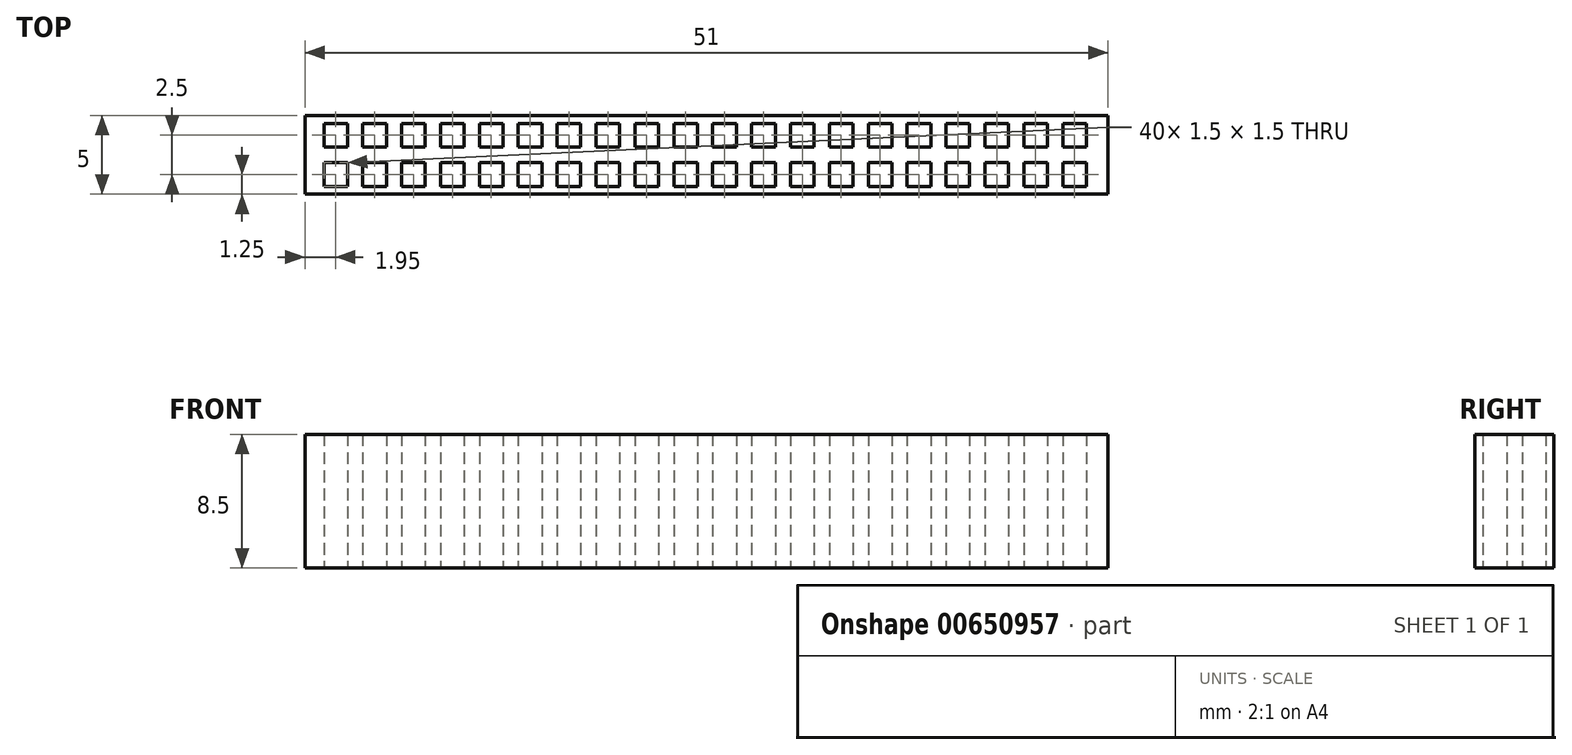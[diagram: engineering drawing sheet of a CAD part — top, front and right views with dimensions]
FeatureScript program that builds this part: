
annotation { "Feature Type Name" : "Feature", "Feature Type Description" : "" }
export const myFeature = defineFeature(function(context is Context, id is Id, definition is map)
    precondition{}
    {
        {
            var Q0;
            Q0=qCreatedBy(makeId("Top.planeOp"),FACE);
            var sketch = newSketch(context, id + "F0", { "sketchPlane" : qUnion([Q0])});
            skLineSegment(sketch, "E0.bottom", {"start": v(0, 0) * mm, "end": v(51, 0) * mm});
            skLineSegment(sketch, "E0.top", {"start": v(0, 5) * mm, "end": v(51, 5) * mm});
            skLineSegment(sketch, "E0.left", {"start": v(0, 0) * mm, "end": v(0, 5) * mm});
            skLineSegment(sketch, "E0.right", {"start": v(51, 0) * mm, "end": v(51, 5) * mm});
            skLineSegment(sketch, "E1.bottom", {"start": v(1.2, 0.5) * mm, "end": v(2.7, 0.5) * mm});
            skLineSegment(sketch, "E1.top", {"start": v(1.2, 2) * mm, "end": v(2.7, 2) * mm});
            skLineSegment(sketch, "E1.left", {"start": v(1.2, 0.5) * mm, "end": v(1.2, 2) * mm});
            skLineSegment(sketch, "E1.right", {"start": v(2.7, 0.5) * mm, "end": v(2.7, 2) * mm});
            skLineSegment(sketch, "E2.0.1.0", {"start": v(1.2, 3) * mm, "end": v(2.7, 3) * mm});
            skLineSegment(sketch, "E2.0.1.1", {"start": v(2.7, 3) * mm, "end": v(2.7, 4.5) * mm});
            skLineSegment(sketch, "E2.0.1.2", {"start": v(1.2, 4.5) * mm, "end": v(2.7, 4.5) * mm});
            skLineSegment(sketch, "E2.0.1.3", {"start": v(1.2, 3) * mm, "end": v(1.2, 4.5) * mm});
            skLineSegment(sketch, "E2.1.0.0", {"start": v(3.67, 0.5) * mm, "end": v(5.17, 0.5) * mm});
            skLineSegment(sketch, "E2.1.0.1", {"start": v(5.17, 0.5) * mm, "end": v(5.17, 2) * mm});
            skLineSegment(sketch, "E2.1.0.2", {"start": v(3.67, 2) * mm, "end": v(5.17, 2) * mm});
            skLineSegment(sketch, "E2.1.0.3", {"start": v(3.67, 0.5) * mm, "end": v(3.67, 2) * mm});
            skLineSegment(sketch, "E2.1.1.0", {"start": v(3.67, 3) * mm, "end": v(5.17, 3) * mm});
            skLineSegment(sketch, "E2.1.1.1", {"start": v(5.17, 3) * mm, "end": v(5.17, 4.5) * mm});
            skLineSegment(sketch, "E2.1.1.2", {"start": v(3.67, 4.5) * mm, "end": v(5.17, 4.5) * mm});
            skLineSegment(sketch, "E2.1.1.3", {"start": v(3.67, 3) * mm, "end": v(3.67, 4.5) * mm});
            skLineSegment(sketch, "E2.2.0.0", {"start": v(6.14, 0.5) * mm, "end": v(7.64, 0.5) * mm});
            skLineSegment(sketch, "E2.2.0.1", {"start": v(7.64, 0.5) * mm, "end": v(7.64, 2) * mm});
            skLineSegment(sketch, "E2.2.0.2", {"start": v(6.14, 2) * mm, "end": v(7.64, 2) * mm});
            skLineSegment(sketch, "E2.2.0.3", {"start": v(6.14, 0.5) * mm, "end": v(6.14, 2) * mm});
            skLineSegment(sketch, "E2.2.1.0", {"start": v(6.14, 3) * mm, "end": v(7.64, 3) * mm});
            skLineSegment(sketch, "E2.2.1.1", {"start": v(7.64, 3) * mm, "end": v(7.64, 4.5) * mm});
            skLineSegment(sketch, "E2.2.1.2", {"start": v(6.14, 4.5) * mm, "end": v(7.64, 4.5) * mm});
            skLineSegment(sketch, "E2.2.1.3", {"start": v(6.14, 3) * mm, "end": v(6.14, 4.5) * mm});
            skLineSegment(sketch, "E2.direction1", {"start": v(1.2, 0.5) * mm, "end": v(3.67, 0.5) * mm, "construction": true});
            skLineSegment(sketch, "E2.direction2", {"start": v(1.2, 0.5) * mm, "end": v(1.2, 3) * mm, "construction": true});
            skLineSegment(sketch, "E3.0.3.0", {"start": v(8.61, 0.5) * mm, "end": v(10.11, 0.5) * mm});
            skLineSegment(sketch, "E3.3.3.0", {"start": v(10.11, 0.5) * mm, "end": v(10.11, 2) * mm});
            skLineSegment(sketch, "E3.6.3.0", {"start": v(8.61, 2) * mm, "end": v(10.11, 2) * mm});
            skLineSegment(sketch, "E3.9.3.0", {"start": v(8.61, 0.5) * mm, "end": v(8.61, 2) * mm});
            skLineSegment(sketch, "E3.0.3.1", {"start": v(8.61, 3) * mm, "end": v(10.11, 3) * mm});
            skLineSegment(sketch, "E3.3.3.1", {"start": v(10.11, 3) * mm, "end": v(10.11, 4.5) * mm});
            skLineSegment(sketch, "E3.6.3.1", {"start": v(8.61, 4.5) * mm, "end": v(10.11, 4.5) * mm});
            skLineSegment(sketch, "E3.9.3.1", {"start": v(8.61, 3) * mm, "end": v(8.61, 4.5) * mm});
            skLineSegment(sketch, "E3.0.4.0", {"start": v(11.08, 0.5) * mm, "end": v(12.58, 0.5) * mm});
            skLineSegment(sketch, "E3.3.4.0", {"start": v(12.58, 0.5) * mm, "end": v(12.58, 2) * mm});
            skLineSegment(sketch, "E3.6.4.0", {"start": v(11.08, 2) * mm, "end": v(12.58, 2) * mm});
            skLineSegment(sketch, "E3.9.4.0", {"start": v(11.08, 0.5) * mm, "end": v(11.08, 2) * mm});
            skLineSegment(sketch, "E3.0.4.1", {"start": v(11.08, 3) * mm, "end": v(12.58, 3) * mm});
            skLineSegment(sketch, "E3.3.4.1", {"start": v(12.58, 3) * mm, "end": v(12.58, 4.5) * mm});
            skLineSegment(sketch, "E3.6.4.1", {"start": v(11.08, 4.5) * mm, "end": v(12.58, 4.5) * mm});
            skLineSegment(sketch, "E3.9.4.1", {"start": v(11.08, 3) * mm, "end": v(11.08, 4.5) * mm});
            skLineSegment(sketch, "E3.0.5.0", {"start": v(13.55, 0.5) * mm, "end": v(15.05, 0.5) * mm});
            skLineSegment(sketch, "E3.3.5.0", {"start": v(15.05, 0.5) * mm, "end": v(15.05, 2) * mm});
            skLineSegment(sketch, "E3.6.5.0", {"start": v(13.55, 2) * mm, "end": v(15.05, 2) * mm});
            skLineSegment(sketch, "E3.9.5.0", {"start": v(13.55, 0.5) * mm, "end": v(13.55, 2) * mm});
            skLineSegment(sketch, "E3.0.5.1", {"start": v(13.55, 3) * mm, "end": v(15.05, 3) * mm});
            skLineSegment(sketch, "E3.3.5.1", {"start": v(15.05, 3) * mm, "end": v(15.05, 4.5) * mm});
            skLineSegment(sketch, "E3.6.5.1", {"start": v(13.55, 4.5) * mm, "end": v(15.05, 4.5) * mm});
            skLineSegment(sketch, "E3.9.5.1", {"start": v(13.55, 3) * mm, "end": v(13.55, 4.5) * mm});
            skLineSegment(sketch, "E3.0.6.0", {"start": v(16.02, 0.5) * mm, "end": v(17.52, 0.5) * mm});
            skLineSegment(sketch, "E3.3.6.0", {"start": v(17.52, 0.5) * mm, "end": v(17.52, 2) * mm});
            skLineSegment(sketch, "E3.6.6.0", {"start": v(16.02, 2) * mm, "end": v(17.52, 2) * mm});
            skLineSegment(sketch, "E3.9.6.0", {"start": v(16.02, 0.5) * mm, "end": v(16.02, 2) * mm});
            skLineSegment(sketch, "E3.0.6.1", {"start": v(16.02, 3) * mm, "end": v(17.52, 3) * mm});
            skLineSegment(sketch, "E3.3.6.1", {"start": v(17.52, 3) * mm, "end": v(17.52, 4.5) * mm});
            skLineSegment(sketch, "E3.6.6.1", {"start": v(16.02, 4.5) * mm, "end": v(17.52, 4.5) * mm});
            skLineSegment(sketch, "E3.9.6.1", {"start": v(16.02, 3) * mm, "end": v(16.02, 4.5) * mm});
            skLineSegment(sketch, "E3.0.7.0", {"start": v(18.5, 0.5) * mm, "end": v(20, 0.5) * mm});
            skLineSegment(sketch, "E3.3.7.0", {"start": v(20, 0.5) * mm, "end": v(20, 2) * mm});
            skLineSegment(sketch, "E3.6.7.0", {"start": v(18.5, 2) * mm, "end": v(20, 2) * mm});
            skLineSegment(sketch, "E3.9.7.0", {"start": v(18.5, 0.5) * mm, "end": v(18.5, 2) * mm});
            skLineSegment(sketch, "E3.0.7.1", {"start": v(18.5, 3) * mm, "end": v(20, 3) * mm});
            skLineSegment(sketch, "E3.3.7.1", {"start": v(20, 3) * mm, "end": v(20, 4.5) * mm});
            skLineSegment(sketch, "E3.6.7.1", {"start": v(18.5, 4.5) * mm, "end": v(20, 4.5) * mm});
            skLineSegment(sketch, "E3.9.7.1", {"start": v(18.5, 3) * mm, "end": v(18.5, 4.5) * mm});
            skLineSegment(sketch, "E3.0.8.0", {"start": v(20.96, 0.5) * mm, "end": v(22.46, 0.5) * mm});
            skLineSegment(sketch, "E3.3.8.0", {"start": v(22.46, 0.5) * mm, "end": v(22.46, 2) * mm});
            skLineSegment(sketch, "E3.6.8.0", {"start": v(20.96, 2) * mm, "end": v(22.46, 2) * mm});
            skLineSegment(sketch, "E3.9.8.0", {"start": v(20.96, 0.5) * mm, "end": v(20.96, 2) * mm});
            skLineSegment(sketch, "E3.0.8.1", {"start": v(20.96, 3) * mm, "end": v(22.46, 3) * mm});
            skLineSegment(sketch, "E3.3.8.1", {"start": v(22.46, 3) * mm, "end": v(22.46, 4.5) * mm});
            skLineSegment(sketch, "E3.6.8.1", {"start": v(20.96, 4.5) * mm, "end": v(22.46, 4.5) * mm});
            skLineSegment(sketch, "E3.9.8.1", {"start": v(20.96, 3) * mm, "end": v(20.96, 4.5) * mm});
            skLineSegment(sketch, "E3.0.9.0", {"start": v(23.43, 0.5) * mm, "end": v(24.93, 0.5) * mm});
            skLineSegment(sketch, "E3.3.9.0", {"start": v(24.93, 0.5) * mm, "end": v(24.93, 2) * mm});
            skLineSegment(sketch, "E3.6.9.0", {"start": v(23.43, 2) * mm, "end": v(24.93, 2) * mm});
            skLineSegment(sketch, "E3.9.9.0", {"start": v(23.43, 0.5) * mm, "end": v(23.43, 2) * mm});
            skLineSegment(sketch, "E3.0.9.1", {"start": v(23.43, 3) * mm, "end": v(24.93, 3) * mm});
            skLineSegment(sketch, "E3.3.9.1", {"start": v(24.93, 3) * mm, "end": v(24.93, 4.5) * mm});
            skLineSegment(sketch, "E3.6.9.1", {"start": v(23.43, 4.5) * mm, "end": v(24.93, 4.5) * mm});
            skLineSegment(sketch, "E3.9.9.1", {"start": v(23.43, 3) * mm, "end": v(23.43, 4.5) * mm});
            skLineSegment(sketch, "E3.0.10.0", {"start": v(25.9, 0.5) * mm, "end": v(27.4, 0.5) * mm});
            skLineSegment(sketch, "E3.3.10.0", {"start": v(27.4, 0.5) * mm, "end": v(27.4, 2) * mm});
            skLineSegment(sketch, "E3.6.10.0", {"start": v(25.9, 2) * mm, "end": v(27.4, 2) * mm});
            skLineSegment(sketch, "E3.9.10.0", {"start": v(25.9, 0.5) * mm, "end": v(25.9, 2) * mm});
            skLineSegment(sketch, "E3.0.10.1", {"start": v(25.9, 3) * mm, "end": v(27.4, 3) * mm});
            skLineSegment(sketch, "E3.3.10.1", {"start": v(27.4, 3) * mm, "end": v(27.4, 4.5) * mm});
            skLineSegment(sketch, "E3.6.10.1", {"start": v(25.9, 4.5) * mm, "end": v(27.4, 4.5) * mm});
            skLineSegment(sketch, "E3.9.10.1", {"start": v(25.9, 3) * mm, "end": v(25.9, 4.5) * mm});
            skLineSegment(sketch, "E3.0.11.0", {"start": v(28.37, 0.5) * mm, "end": v(29.87, 0.5) * mm});
            skLineSegment(sketch, "E3.3.11.0", {"start": v(29.87, 0.5) * mm, "end": v(29.87, 2) * mm});
            skLineSegment(sketch, "E3.6.11.0", {"start": v(28.37, 2) * mm, "end": v(29.87, 2) * mm});
            skLineSegment(sketch, "E3.9.11.0", {"start": v(28.37, 0.5) * mm, "end": v(28.37, 2) * mm});
            skLineSegment(sketch, "E3.0.11.1", {"start": v(28.37, 3) * mm, "end": v(29.87, 3) * mm});
            skLineSegment(sketch, "E3.3.11.1", {"start": v(29.87, 3) * mm, "end": v(29.87, 4.5) * mm});
            skLineSegment(sketch, "E3.6.11.1", {"start": v(28.37, 4.5) * mm, "end": v(29.87, 4.5) * mm});
            skLineSegment(sketch, "E3.9.11.1", {"start": v(28.37, 3) * mm, "end": v(28.37, 4.5) * mm});
            skLineSegment(sketch, "E3.0.12.0", {"start": v(30.84, 0.5) * mm, "end": v(32.34, 0.5) * mm});
            skLineSegment(sketch, "E3.3.12.0", {"start": v(32.34, 0.5) * mm, "end": v(32.34, 2) * mm});
            skLineSegment(sketch, "E3.6.12.0", {"start": v(30.84, 2) * mm, "end": v(32.34, 2) * mm});
            skLineSegment(sketch, "E3.9.12.0", {"start": v(30.84, 0.5) * mm, "end": v(30.84, 2) * mm});
            skLineSegment(sketch, "E3.0.12.1", {"start": v(30.84, 3) * mm, "end": v(32.34, 3) * mm});
            skLineSegment(sketch, "E3.3.12.1", {"start": v(32.34, 3) * mm, "end": v(32.34, 4.5) * mm});
            skLineSegment(sketch, "E3.6.12.1", {"start": v(30.84, 4.5) * mm, "end": v(32.34, 4.5) * mm});
            skLineSegment(sketch, "E3.9.12.1", {"start": v(30.84, 3) * mm, "end": v(30.84, 4.5) * mm});
            skLineSegment(sketch, "E3.0.13.0", {"start": v(33.31, 0.5) * mm, "end": v(34.81, 0.5) * mm});
            skLineSegment(sketch, "E3.3.13.0", {"start": v(34.81, 0.5) * mm, "end": v(34.81, 2) * mm});
            skLineSegment(sketch, "E3.6.13.0", {"start": v(33.31, 2) * mm, "end": v(34.81, 2) * mm});
            skLineSegment(sketch, "E3.9.13.0", {"start": v(33.31, 0.5) * mm, "end": v(33.31, 2) * mm});
            skLineSegment(sketch, "E3.0.13.1", {"start": v(33.31, 3) * mm, "end": v(34.81, 3) * mm});
            skLineSegment(sketch, "E3.3.13.1", {"start": v(34.81, 3) * mm, "end": v(34.81, 4.5) * mm});
            skLineSegment(sketch, "E3.6.13.1", {"start": v(33.31, 4.5) * mm, "end": v(34.81, 4.5) * mm});
            skLineSegment(sketch, "E3.9.13.1", {"start": v(33.31, 3) * mm, "end": v(33.31, 4.5) * mm});
            skLineSegment(sketch, "E3.0.14.0", {"start": v(35.78, 0.5) * mm, "end": v(37.28, 0.5) * mm});
            skLineSegment(sketch, "E3.3.14.0", {"start": v(37.28, 0.5) * mm, "end": v(37.28, 2) * mm});
            skLineSegment(sketch, "E3.6.14.0", {"start": v(35.78, 2) * mm, "end": v(37.28, 2) * mm});
            skLineSegment(sketch, "E3.9.14.0", {"start": v(35.78, 0.5) * mm, "end": v(35.78, 2) * mm});
            skLineSegment(sketch, "E3.0.14.1", {"start": v(35.78, 3) * mm, "end": v(37.28, 3) * mm});
            skLineSegment(sketch, "E3.3.14.1", {"start": v(37.28, 3) * mm, "end": v(37.28, 4.5) * mm});
            skLineSegment(sketch, "E3.6.14.1", {"start": v(35.78, 4.5) * mm, "end": v(37.28, 4.5) * mm});
            skLineSegment(sketch, "E3.9.14.1", {"start": v(35.78, 3) * mm, "end": v(35.78, 4.5) * mm});
            skLineSegment(sketch, "E3.0.15.0", {"start": v(38.25, 0.5) * mm, "end": v(39.75, 0.5) * mm});
            skLineSegment(sketch, "E3.3.15.0", {"start": v(39.75, 0.5) * mm, "end": v(39.75, 2) * mm});
            skLineSegment(sketch, "E3.6.15.0", {"start": v(38.25, 2) * mm, "end": v(39.75, 2) * mm});
            skLineSegment(sketch, "E3.9.15.0", {"start": v(38.25, 0.5) * mm, "end": v(38.25, 2) * mm});
            skLineSegment(sketch, "E3.0.15.1", {"start": v(38.25, 3) * mm, "end": v(39.75, 3) * mm});
            skLineSegment(sketch, "E3.3.15.1", {"start": v(39.75, 3) * mm, "end": v(39.75, 4.5) * mm});
            skLineSegment(sketch, "E3.6.15.1", {"start": v(38.25, 4.5) * mm, "end": v(39.75, 4.5) * mm});
            skLineSegment(sketch, "E3.9.15.1", {"start": v(38.25, 3) * mm, "end": v(38.25, 4.5) * mm});
            skLineSegment(sketch, "E3.0.16.0", {"start": v(40.72, 0.5) * mm, "end": v(42.22, 0.5) * mm});
            skLineSegment(sketch, "E3.3.16.0", {"start": v(42.22, 0.5) * mm, "end": v(42.22, 2) * mm});
            skLineSegment(sketch, "E3.6.16.0", {"start": v(40.72, 2) * mm, "end": v(42.22, 2) * mm});
            skLineSegment(sketch, "E3.9.16.0", {"start": v(40.72, 0.5) * mm, "end": v(40.72, 2) * mm});
            skLineSegment(sketch, "E3.0.16.1", {"start": v(40.72, 3) * mm, "end": v(42.22, 3) * mm});
            skLineSegment(sketch, "E3.3.16.1", {"start": v(42.22, 3) * mm, "end": v(42.22, 4.5) * mm});
            skLineSegment(sketch, "E3.6.16.1", {"start": v(40.72, 4.5) * mm, "end": v(42.22, 4.5) * mm});
            skLineSegment(sketch, "E3.9.16.1", {"start": v(40.72, 3) * mm, "end": v(40.72, 4.5) * mm});
            skLineSegment(sketch, "E3.0.17.0", {"start": v(43.2, 0.5) * mm, "end": v(44.7, 0.5) * mm});
            skLineSegment(sketch, "E3.3.17.0", {"start": v(44.7, 0.5) * mm, "end": v(44.7, 2) * mm});
            skLineSegment(sketch, "E3.6.17.0", {"start": v(43.2, 2) * mm, "end": v(44.7, 2) * mm});
            skLineSegment(sketch, "E3.9.17.0", {"start": v(43.2, 0.5) * mm, "end": v(43.2, 2) * mm});
            skLineSegment(sketch, "E3.0.17.1", {"start": v(43.2, 3) * mm, "end": v(44.7, 3) * mm});
            skLineSegment(sketch, "E3.3.17.1", {"start": v(44.7, 3) * mm, "end": v(44.7, 4.5) * mm});
            skLineSegment(sketch, "E3.6.17.1", {"start": v(43.2, 4.5) * mm, "end": v(44.7, 4.5) * mm});
            skLineSegment(sketch, "E3.9.17.1", {"start": v(43.2, 3) * mm, "end": v(43.2, 4.5) * mm});
            skLineSegment(sketch, "E3.0.18.0", {"start": v(45.66, 0.5) * mm, "end": v(47.16, 0.5) * mm});
            skLineSegment(sketch, "E3.3.18.0", {"start": v(47.16, 0.5) * mm, "end": v(47.16, 2) * mm});
            skLineSegment(sketch, "E3.6.18.0", {"start": v(45.66, 2) * mm, "end": v(47.16, 2) * mm});
            skLineSegment(sketch, "E3.9.18.0", {"start": v(45.66, 0.5) * mm, "end": v(45.66, 2) * mm});
            skLineSegment(sketch, "E3.0.18.1", {"start": v(45.66, 3) * mm, "end": v(47.16, 3) * mm});
            skLineSegment(sketch, "E3.3.18.1", {"start": v(47.16, 3) * mm, "end": v(47.16, 4.5) * mm});
            skLineSegment(sketch, "E3.6.18.1", {"start": v(45.66, 4.5) * mm, "end": v(47.16, 4.5) * mm});
            skLineSegment(sketch, "E3.9.18.1", {"start": v(45.66, 3) * mm, "end": v(45.66, 4.5) * mm});
            skLineSegment(sketch, "E3.0.19.0", {"start": v(48.13, 0.5) * mm, "end": v(49.63, 0.5) * mm});
            skLineSegment(sketch, "E3.3.19.0", {"start": v(49.63, 0.5) * mm, "end": v(49.63, 2) * mm});
            skLineSegment(sketch, "E3.6.19.0", {"start": v(48.13, 2) * mm, "end": v(49.63, 2) * mm});
            skLineSegment(sketch, "E3.9.19.0", {"start": v(48.13, 0.5) * mm, "end": v(48.13, 2) * mm});
            skLineSegment(sketch, "E3.0.19.1", {"start": v(48.13, 3) * mm, "end": v(49.63, 3) * mm});
            skLineSegment(sketch, "E3.3.19.1", {"start": v(49.63, 3) * mm, "end": v(49.63, 4.5) * mm});
            skLineSegment(sketch, "E3.6.19.1", {"start": v(48.13, 4.5) * mm, "end": v(49.63, 4.5) * mm});
            skLineSegment(sketch, "E3.9.19.1", {"start": v(48.13, 3) * mm, "end": v(48.13, 4.5) * mm});
            skSolve(sketch);
        }
        {
            var Q0;
            Q0=makeQuery(id+"F0.imprint","IMPRINT",FACE,{"disambiguationData":[TD([[makeQuery(id+"F0.imprint","IMPRINT",EDGE,{"derivedFrom":sQuery(id+"F0.wireOp",EDGE,"E0.bottom")}),1.0]])]});
            extrude(context, id + "F1", {"entities" : qUnion([Q0]), "depth" : 8.5 * mm, "offsetDistance" : 25 * mm});
        }
    });
